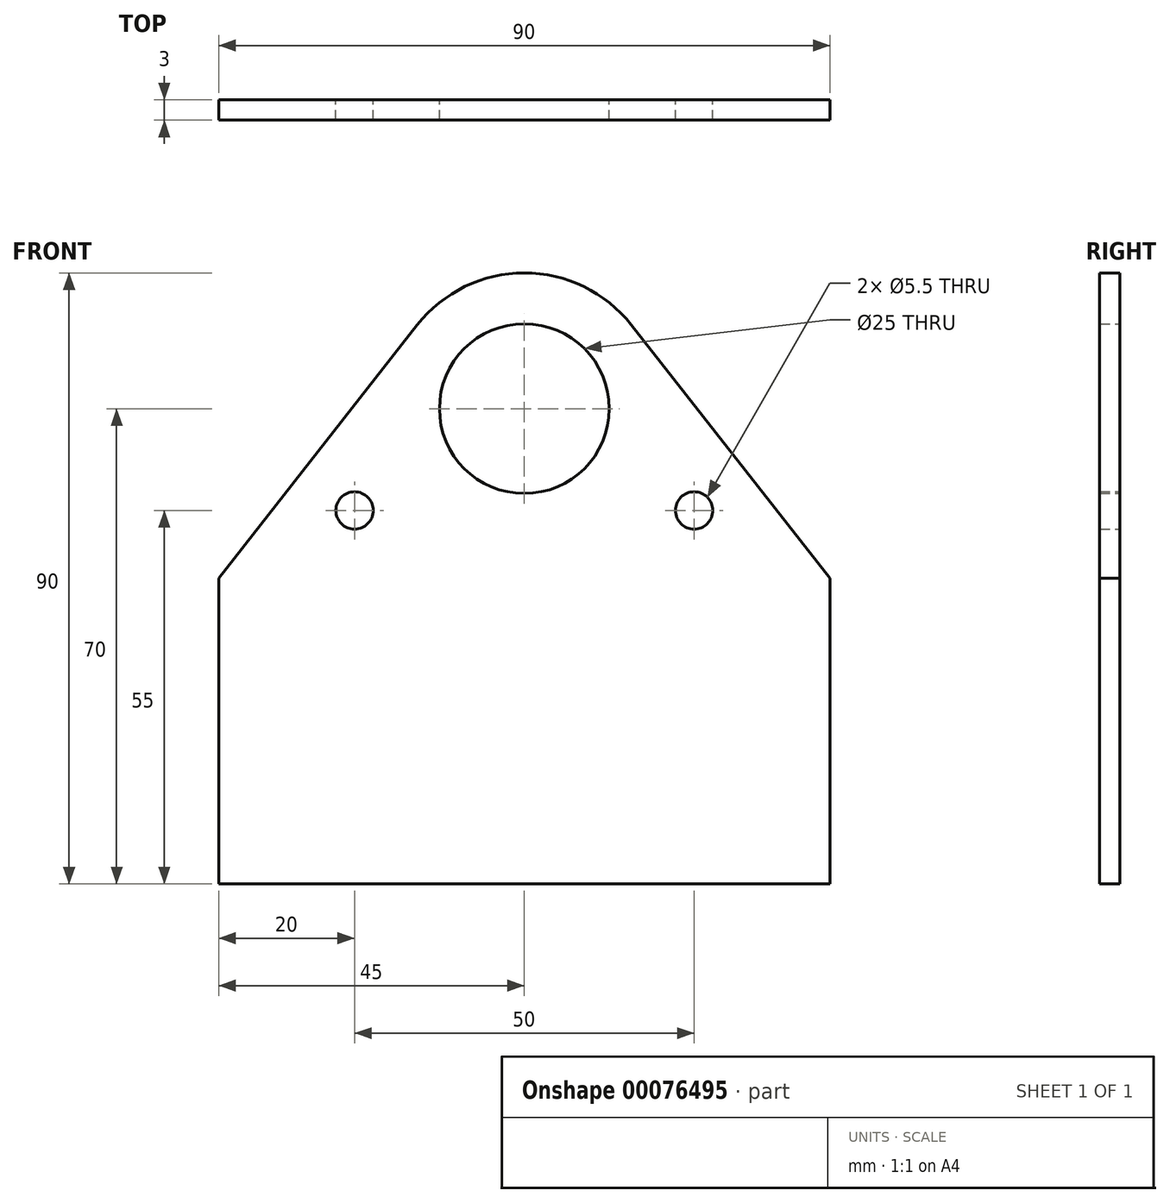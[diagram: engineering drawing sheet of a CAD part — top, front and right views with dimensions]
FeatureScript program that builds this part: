
annotation { "Feature Type Name" : "Feature", "Feature Type Description" : "" }
export const myFeature = defineFeature(function(context is Context, id is Id, definition is map)
    precondition{}
    {
        {
            var Q0;
            Q0=qCreatedBy(makeId("Front.planeOp"),FACE);
            var sketch = newSketch(context, id + "F0", { "sketchPlane" : qUnion([Q0])});
            skCircle(sketch, "E0", {"center": v(0, 0) * mm, "radius": 12.5 * mm});
            skArc(sketch, "E1", {"start": v(15.74, 12.34) * mm, "mid": v(0, 20) * mm, "end": v(-15.74, 12.34) * mm});
            skLineSegment(sketch, "E2.top", {"start": v(-45, -70) * mm, "end": v(45, -70) * mm});
            skLineSegment(sketch, "E2.left", {"start": v(-45, -25) * mm, "end": v(-45, -70) * mm});
            skLineSegment(sketch, "E2.right", {"start": v(45, -25) * mm, "end": v(45, -70) * mm});
            skLineSegment(sketch, "E3", {"start": v(-45, -25) * mm, "end": v(-15.74, 12.34) * mm});
            skLineSegment(sketch, "E4", {"start": v(45, -25) * mm, "end": v(15.74, 12.34) * mm});
            skCircle(sketch, "E5", {"center": v(-25, -15) * mm, "radius": 2.75 * mm});
            skCircle(sketch, "E6", {"center": v(25, -15) * mm, "radius": 2.75 * mm});
            skSolve(sketch);
        }
        {
            var Q0;
            Q0 = qSketchRegion(id + "F0", true);
            extrude(context, id + "F1", {"entities" : qUnion([Q0]), "depth" : 3 * mm});
        }
    });
